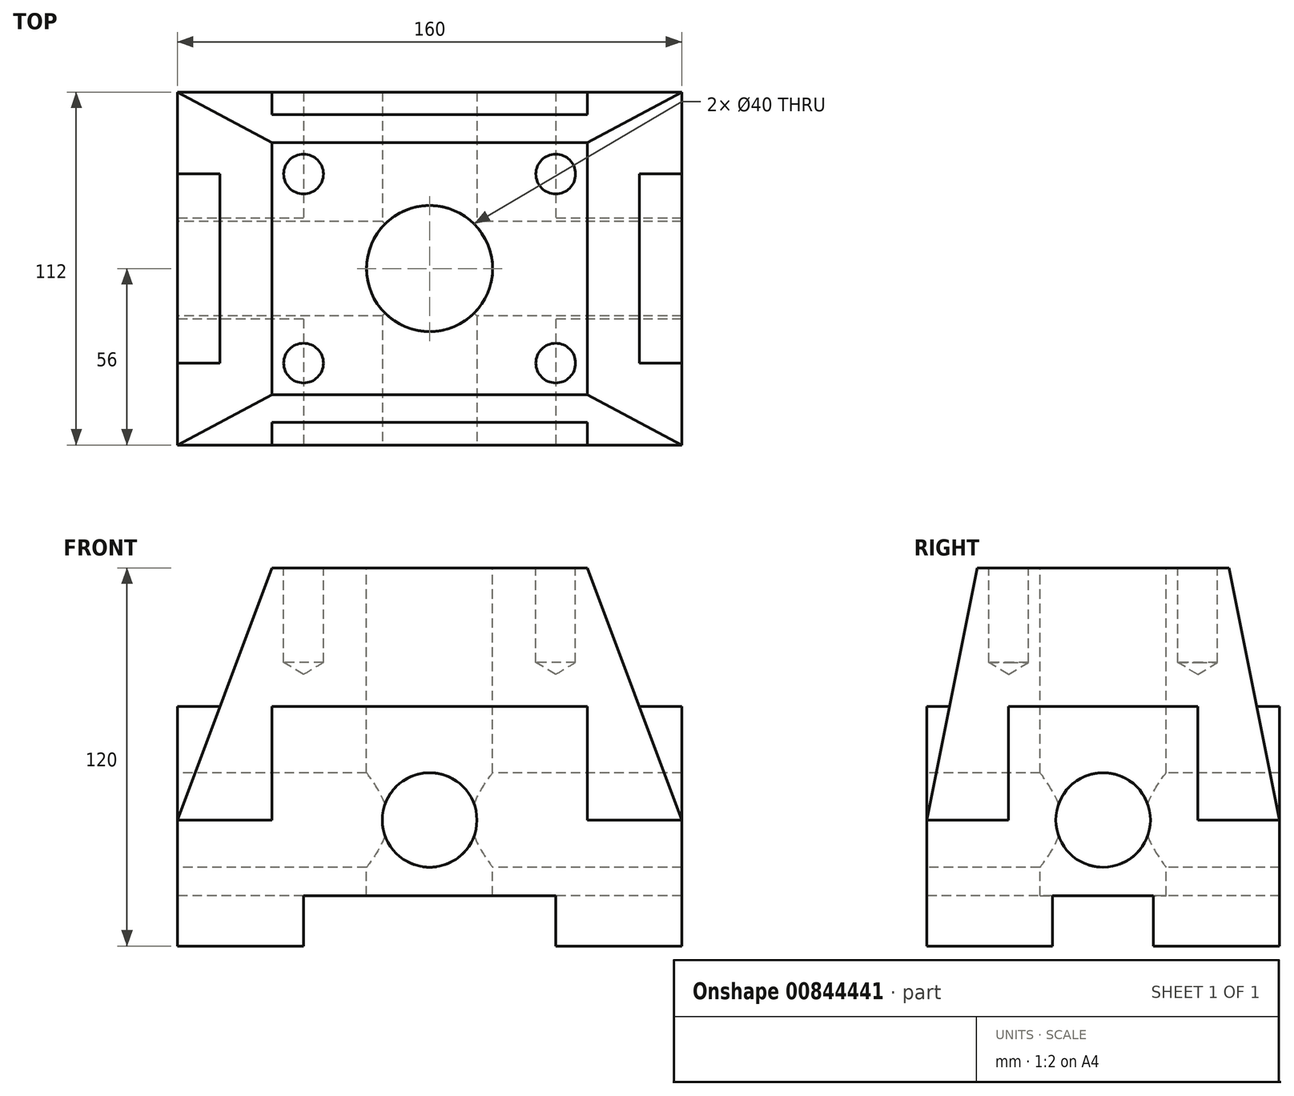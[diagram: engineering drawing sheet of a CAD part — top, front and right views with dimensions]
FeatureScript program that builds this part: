
annotation { "Feature Type Name" : "Feature", "Feature Type Description" : "" }
export const myFeature = defineFeature(function(context is Context, id is Id, definition is map)
    precondition{}
    {
        {
            var Q0;
            Q0=qCreatedBy(makeId("Top.planeOp"),FACE);
            var sketch = newSketch(context, id + "F0", { "sketchPlane" : qUnion([Q0])});
            skLineSegment(sketch, "E0.bottom", {"start": v(80, 56) * mm, "end": v(-80, 56) * mm});
            skLineSegment(sketch, "E0.top", {"start": v(80, -56) * mm, "end": v(-80, -56) * mm});
            skLineSegment(sketch, "E0.left", {"start": v(80, 56) * mm, "end": v(80, -56) * mm});
            skLineSegment(sketch, "E0.right", {"start": v(-80, 56) * mm, "end": v(-80, -56) * mm});
            skPoint(sketch, "E0.middle", {"position": v(0, 0) * mm});
            skSolve(sketch);
        }
        {
            var Q0;
            Q0 = qSketchRegion(id + "F0", true);
            extrude(context, id + "F1", {"entities" : qUnion([Q0]), "oppositeDirection" : true, "depth" : 40 * mm, "offsetDistance" : 25 * mm});
        }
        {
            var Q0;
            Q0=makeQuery(id+"F1.opExtrude","SWEPT_FACE",FACE,{"disambiguationData":[OSD([sQuery(id+"F0.wireOp",EDGE,"E0.top")])]});
            var sketch = newSketch(context, id + "F2", { "sketchPlane" : qUnion([Q0])});
            skLineSegment(sketch, "E1.bottom", {"start": v(-40, -40) * mm, "end": v(40, -40) * mm});
            skLineSegment(sketch, "E1.top", {"start": v(-40, -24) * mm, "end": v(40, -24) * mm});
            skLineSegment(sketch, "E1.left", {"start": v(-40, -40) * mm, "end": v(-40, -24) * mm});
            skLineSegment(sketch, "E1.right", {"start": v(40, -40) * mm, "end": v(40, -24) * mm});
            skSolve(sketch);
        }
        {
            var Q0;
            Q0 = qSketchRegion(id + "F2", true);
            extrude(context, id + "F3", {"entities" : qUnion([Q0]), "operationType" : NewBodyOperationType.REMOVE, "oppositeDirection" : true, "depth" : 115 * mm, "offsetDistance" : 25 * mm});
        }
        {
            var Q0;
            Q0=makeQuery(id+"F1.opExtrude","SWEPT_FACE",FACE,{"disambiguationData":[OSD([sQuery(id+"F0.wireOp",EDGE,"E0.right")])]});
            var sketch = newSketch(context, id + "F4", { "sketchPlane" : qUnion([Q0])});
            skLineSegment(sketch, "E2.bottom", {"start": v(-16, -40) * mm, "end": v(16, -40) * mm});
            skLineSegment(sketch, "E2.top", {"start": v(-16, -24) * mm, "end": v(16, -24) * mm});
            skLineSegment(sketch, "E2.left", {"start": v(-16, -40) * mm, "end": v(-16, -24) * mm});
            skLineSegment(sketch, "E2.right", {"start": v(16, -40) * mm, "end": v(16, -24) * mm});
            skSolve(sketch);
        }
        {
            var Q0;
            Q0 = qSketchRegion(id + "F4", true);
            extrude(context, id + "F5", {"entities" : qUnion([Q0]), "operationType" : NewBodyOperationType.REMOVE, "oppositeDirection" : true, "depth" : 165 * mm, "offsetDistance" : 25 * mm});
        }
        {
            var Q0;
            Q0=makeQuery(id+"F1.opExtrude","CAP_FACE",FACE,{"disambiguationData":[OSD([sQuery(id+"F0.wireOp",EDGE,"E0.bottom"),sQuery(id+"F0.wireOp",EDGE,"E0.top"),sQuery(id+"F0.wireOp",EDGE,"E0.left"),sQuery(id+"F0.wireOp",EDGE,"E0.right")])],"isStart":true});
            var sketch = newSketch(context, id + "F6", { "sketchPlane" : qUnion([Q0])});
            skLineSegment(sketch, "E3.bottom", {"start": v(-50, 56) * mm, "end": v(50, 56) * mm});
            skLineSegment(sketch, "E3.top", {"start": v(-50, -56) * mm, "end": v(50, -56) * mm});
            skLineSegment(sketch, "E3.left", {"start": v(-50, 56) * mm, "end": v(-50, -56) * mm});
            skLineSegment(sketch, "E3.right", {"start": v(50, 56) * mm, "end": v(50, -56) * mm});
            skSolve(sketch);
        }
        {
            var Q0;
            Q0 = qSketchRegion(id + "F6", true);
            extrude(context, id + "F7", {"entities" : qUnion([Q0]), "operationType" : NewBodyOperationType.ADD, "depth" : 36 * mm, "offsetDistance" : 25 * mm});
        }
        {
            var Q0;
            {var subQ0=sQuery(id+"F0.wireOp",EDGE,"E0.bottom");var subQ1=sQuery(id+"F0.wireOp",EDGE,"E0.left");var subQ2=sQuery(id+"F0.wireOp",EDGE,"E0.top");Q0=makeQuery(id+"F7.boolean.opBoolean","SPLIT",FACE,{"disambiguationData":[TD([makeQuery(id+"F1.opExtrude","SWEPT_FACE",FACE,{"disambiguationData":[OSD([subQ1])]})])],"derivedFrom":makeQuery(id+"F1.opExtrude","CAP_FACE",FACE,{"disambiguationData":[OSD([subQ0,subQ2,subQ1,sQuery(id+"F0.wireOp",EDGE,"E0.right")])],"isStart":true})});}
            var sketch = newSketch(context, id + "F8", { "sketchPlane" : qUnion([Q0])});
            skLineSegment(sketch, "E4.bottom", {"start": v(50, 30) * mm, "end": v(80, 30) * mm});
            skLineSegment(sketch, "E4.top", {"start": v(50, -30) * mm, "end": v(80, -30) * mm});
            skLineSegment(sketch, "E4.left", {"start": v(50, 30) * mm, "end": v(50, -30) * mm});
            skLineSegment(sketch, "E4.right", {"start": v(80, 30) * mm, "end": v(80, -30) * mm});
            skSolve(sketch);
        }
        {
            var Q0;
            Q0 = qSketchRegion(id + "F8", true);
            extrude(context, id + "F9", {"entities" : qUnion([Q0]), "operationType" : NewBodyOperationType.ADD, "depth" : 36 * mm, "offsetDistance" : 25 * mm});
        }
        {
            var Q0;
            {var subQ0=sQuery(id+"F0.wireOp",EDGE,"E0.bottom");var subQ1=sQuery(id+"F0.wireOp",EDGE,"E0.top");var subQ2=sQuery(id+"F0.wireOp",EDGE,"E0.right");Q0=makeQuery(id+"F7.boolean.opBoolean","SPLIT",FACE,{"disambiguationData":[TD([makeQuery(id+"F1.opExtrude","SWEPT_FACE",FACE,{"disambiguationData":[OSD([subQ2])]})])],"derivedFrom":makeQuery(id+"F1.opExtrude","CAP_FACE",FACE,{"disambiguationData":[OSD([subQ0,subQ1,sQuery(id+"F0.wireOp",EDGE,"E0.left"),subQ2])],"isStart":true})});}
            var sketch = newSketch(context, id + "F10", { "sketchPlane" : qUnion([Q0])});
            skLineSegment(sketch, "E5.bottom", {"start": v(-80, 30) * mm, "end": v(-50, 30) * mm});
            skLineSegment(sketch, "E5.top", {"start": v(-80, -30) * mm, "end": v(-50, -30) * mm});
            skLineSegment(sketch, "E5.left", {"start": v(-80, 30) * mm, "end": v(-80, -30) * mm});
            skLineSegment(sketch, "E5.right", {"start": v(-50, 30) * mm, "end": v(-50, -30) * mm});
            skSolve(sketch);
        }
        {
            var Q0;
            Q0 = qSketchRegion(id + "F10", true);
            extrude(context, id + "F11", {"entities" : qUnion([Q0]), "operationType" : NewBodyOperationType.ADD, "depth" : 36 * mm, "offsetDistance" : 25 * mm});
        }
        {
            var Q0;
            Q0=qCreatedBy(makeId("Top.planeOp"),FACE);
            var sketch = newSketch(context, id + "F12", { "sketchPlane" : qUnion([Q0])});
            skLineSegment(sketch, "E6.bottom", {"start": v(80, 56) * mm, "end": v(-80, 56) * mm});
            skLineSegment(sketch, "E6.top", {"start": v(80, -56) * mm, "end": v(-80, -56) * mm});
            skLineSegment(sketch, "E6.left", {"start": v(80, 56) * mm, "end": v(80, -56) * mm});
            skLineSegment(sketch, "E6.right", {"start": v(-80, 56) * mm, "end": v(-80, -56) * mm});
            skPoint(sketch, "E6.middle", {"position": v(0, 0) * mm});
            skSolve(sketch);
        }
        {
            var Q0;
            Q0=qCreatedBy(makeId("Top.planeOp"),FACE);
            cPlane(context, id + "F13", {"entities" : qUnion([Q0]), "cplaneType" : CPlaneType.OFFSET, "offset" : 80 * mm, "width" : 150 * mm, "height" : 150 * mm});
        }
        {
            var Q0;
            Q0=qCreatedBy(id+"F13.planeOp",FACE);
            var sketch = newSketch(context, id + "F14", { "sketchPlane" : qUnion([Q0])});
            skLineSegment(sketch, "E7.bottom", {"start": v(50, 40) * mm, "end": v(-50, 40) * mm});
            skLineSegment(sketch, "E7.top", {"start": v(50, -40) * mm, "end": v(-50, -40) * mm});
            skLineSegment(sketch, "E7.left", {"start": v(50, 40) * mm, "end": v(50, -40) * mm});
            skLineSegment(sketch, "E7.right", {"start": v(-50, 40) * mm, "end": v(-50, -40) * mm});
            skPoint(sketch, "E7.middle", {"position": v(0, 0) * mm});
            skSolve(sketch);
        }
        {
            var Q1;
            Q1=makeQuery(id+"F14.imprint","IMPRINT",FACE,{"disambiguationData":[TD([[makeQuery(id+"F14.imprint","IMPRINT",EDGE,{"derivedFrom":sQuery(id+"F14.wireOp",EDGE,"E7.bottom")}),1.0]])]});
            var Q2;
            Q2=makeQuery(id+"F12.imprint","IMPRINT",FACE,{"disambiguationData":[TD([[makeQuery(id+"F12.imprint","IMPRINT",EDGE,{"derivedFrom":sQuery(id+"F12.wireOp",EDGE,"E6.bottom")}),1.0]])]});
            loft(context, id + "F15", {"operationType" : NewBodyOperationType.ADD, "sheetProfilesArray" : [{ "sheetProfileEntities" : qUnion([Q1]) }, { "sheetProfileEntities" : qUnion([Q2]) }]});
        }
        {
            var Q0;
            Q0=makeQuery(id+"F15.opLoft","CAP_FACE",FACE,{"disambiguationData":[OSD([makeQuery(id+"F14.imprint","IMPRINT",FACE,{"disambiguationData":[TD([[makeQuery(id+"F14.imprint","IMPRINT",EDGE,{"derivedFrom":sQuery(id+"F14.wireOp",EDGE,"E7.bottom")}),1.0]])]})])],"isStart":true});
            var sketch = newSketch(context, id + "F16", { "sketchPlane" : qUnion([Q0])});
            skCircle(sketch, "E8", {"center": v(0, 0) * mm, "radius": 20 * mm});
            skSolve(sketch);
        }
        {
            var Q0;
            Q0 = qSketchRegion(id + "F16", true);
            extrude(context, id + "F17", {"entities" : qUnion([Q0]), "operationType" : NewBodyOperationType.REMOVE, "oppositeDirection" : true, "depth" : 120 * mm, "offsetDistance" : 25 * mm});
        }
        {
            var Q0;
            Q0=makeQuery(id+"F7.boolean.opBoolean","MERGE",FACE,{"derivedFrom":[makeQuery(id+"F1.opExtrude","SWEPT_FACE",FACE,{"disambiguationData":[OSD([sQuery(id+"F0.wireOp",EDGE,"E0.top")])]}),makeQuery(id+"F7.opExtrude","SWEPT_FACE",FACE,{"disambiguationData":[OSD([sQuery(id+"F6.wireOp",EDGE,"E3.top")])]})]});
            var sketch = newSketch(context, id + "F18", { "sketchPlane" : qUnion([Q0])});
            skCircle(sketch, "E9", {"center": v(0, 0) * mm, "radius": 15 * mm});
            skSolve(sketch);
        }
        {
            var Q0;
            Q0 = qSketchRegion(id + "F18", true);
            extrude(context, id + "F19", {"entities" : qUnion([Q0]), "operationType" : NewBodyOperationType.REMOVE, "oppositeDirection" : true, "depth" : 112 * mm, "offsetDistance" : 25 * mm});
        }
        {
            var Q0;
            Q0=makeQuery(id+"F11.boolean.opBoolean","MERGE",FACE,{"derivedFrom":[makeQuery(id+"F1.opExtrude","SWEPT_FACE",FACE,{"disambiguationData":[OSD([sQuery(id+"F0.wireOp",EDGE,"E0.right")])]}),makeQuery(id+"F11.opExtrude","SWEPT_FACE",FACE,{"disambiguationData":[OSD([sQuery(id+"F10.wireOp",EDGE,"E5.left")])]})]});
            var sketch = newSketch(context, id + "F20", { "sketchPlane" : qUnion([Q0])});
            skCircle(sketch, "E10", {"center": v(0, 0) * mm, "radius": 15 * mm});
            skSolve(sketch);
        }
        {
            var Q0;
            Q0 = qSketchRegion(id + "F20", true);
            extrude(context, id + "F21", {"entities" : qUnion([Q0]), "operationType" : NewBodyOperationType.REMOVE, "oppositeDirection" : true, "depth" : 160 * mm, "offsetDistance" : 25 * mm});
        }
        {
            var Q0;
            Q0=makeQuery(id+"F15.opLoft","CAP_FACE",FACE,{"disambiguationData":[OSD([makeQuery(id+"F14.imprint","IMPRINT",FACE,{"disambiguationData":[TD([[makeQuery(id+"F14.imprint","IMPRINT",EDGE,{"derivedFrom":sQuery(id+"F14.wireOp",EDGE,"E7.bottom")}),1.0]])]})])],"isStart":true});
            var sketch = newSketch(context, id + "F22", { "sketchPlane" : qUnion([Q0])});
            skPoint(sketch, "E11", {"position": v(-40, 30) * mm});
            skPoint(sketch, "E12", {"position": v(40, 30) * mm});
            skPoint(sketch, "E13", {"position": v(40, -30) * mm});
            skPoint(sketch, "E14", {"position": v(-40, -30) * mm});
            skSolve(sketch);
        }
        {
            var Q0;
            Q0=sQuery(id+"F22.wireOp",VERTEX,"E11");
            var Q1;
            Q1=sQuery(id+"F22.wireOp",VERTEX,"E12");
            var Q2;
            Q2=sQuery(id+"F22.wireOp",VERTEX,"E13");
            var Q3;
            Q3=sQuery(id+"F22.wireOp",VERTEX,"E14");
            var Q4;
            Q4=makeQuery(id+"F1.opExtrude","SWEPT_BODY",BODY,{"disambiguationData":[OSD([sQuery(id+"F0.wireOp",EDGE,"E0.bottom"),sQuery(id+"F0.wireOp",EDGE,"E0.top"),sQuery(id+"F0.wireOp",EDGE,"E0.left"),sQuery(id+"F0.wireOp",EDGE,"E0.right")])]});
            hole(context, id + "F23", {"style" : HoleStyle.SIMPLE, "endStyle" : HoleEndStyle.BLIND, "standardTappedOrClearance" : lookupTablePath({ "fit" : "Close", "standard" : "ISO", "size" : "M12", "type" : "Clearance" }), "standardBlindInLast" : lookupTablePath({ "fit" : "Close", "standard" : "ISO", "size" : "M12", "type" : "Clearance" }), "holeDiameter" : 12.6 * mm, "majorDiameter" : 5 * mm, "holeDepth" : 30 * mm, "isTappedThrough" : true, "tappedDepth" : 12 * mm, "tapClearance" : 3, "startFromSketch" : true, "locations" : qUnion([Q0, Q1, Q2, Q3]), "scope" : qUnion([Q4])});
        }
    });
